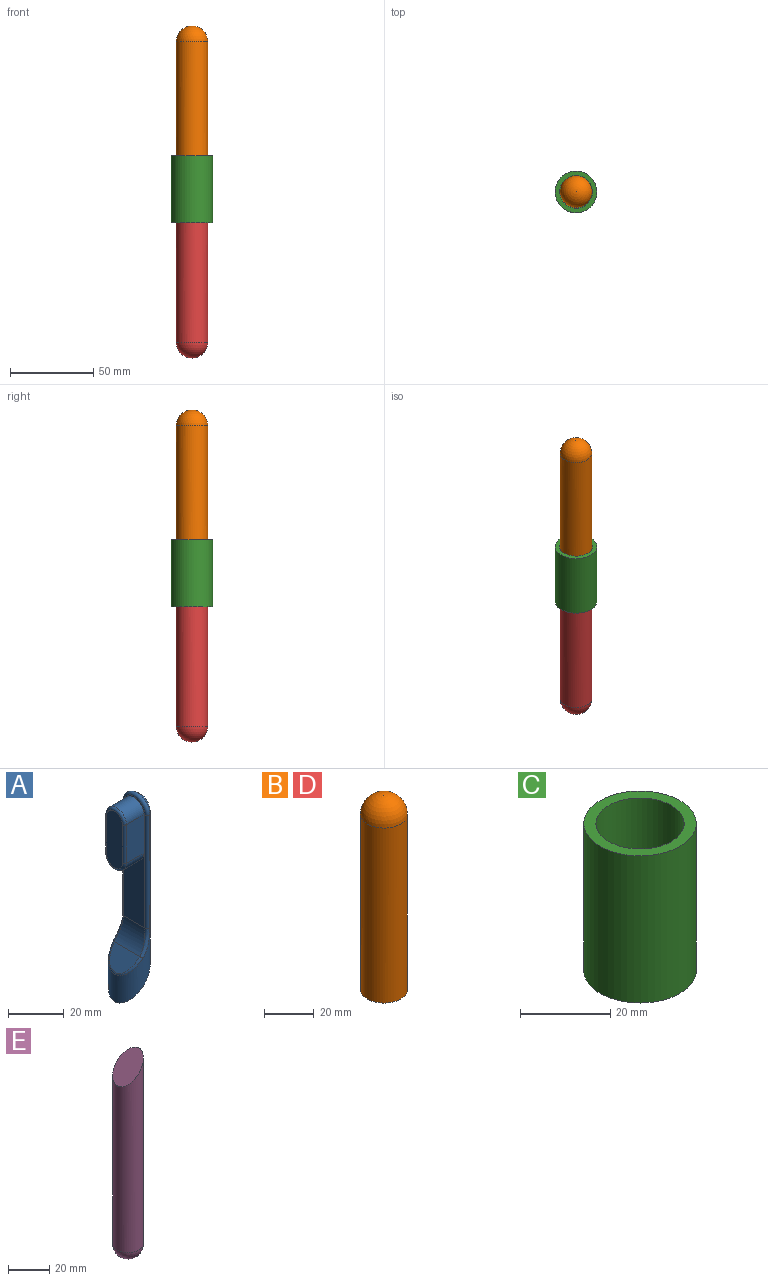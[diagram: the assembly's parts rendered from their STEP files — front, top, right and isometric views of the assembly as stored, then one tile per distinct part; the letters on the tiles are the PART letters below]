
ASSEMBLY  parts=5 mates=4
PART A: 21 faces, bbox 15x15.1x87 mm
  f0: plane 55.28x10.95mm, normal (-1,0,0), area 344.1mm2, adj f4,f5,f7,f9,f12,f13,f14,f15
  f1: cylinder r=7.5mm len=80mm, axis (0,0,-1), area 1400.2mm2, adj f2,f5,f6,f8,f9,f10,f11
  f2: sphere r=7.5mm, area 81.6mm2, adj f1,f7
  f3: plane 12.97x7.21mm, normal (-0.77,0,0.64), area 94.1mm2, adj f4,f8
  f4: cylinder r=15.89mm len=13mm, axis (0,1,0), area 133.2mm2, adj f0,f3,f6,f10
  f5: cylinder r=1mm len=49.8mm, axis (0,0,-1), area 106.5mm2, adj f0,f1,f6,f7
  f6: bspline ~13.34x6.03mm, area 21.9mm2, adj f1,f4,f5,f8
  f7: torus R=5.48mm, axis (1,0,0), area 41.6mm2, adj f0,f2,f5,f9
  f8: bspline ~14.96x7.85mm, area 27.7mm2, adj f1,f3,f6,f10
  f9: cylinder r=1mm len=49.8mm, axis (0,0,-1), area 106.5mm2, adj f0,f1,f7,f10
  f10: bspline ~13.34x6.03mm, area 21.9mm2, adj f1,f4,f8,f9
  f11: plane 15x15mm, normal (0.71,0,-0.71), area 249.9mm2, adj f1
  f12: plane 17x9mm, normal (0,-1,0), area 153mm2, adj f0,f13,f15,f17
  f13: cylinder r=5mm len=10mm, axis (1,0,0), area 141.4mm2, adj f0,f12,f14,f18
  f14: plane 17x9mm, normal (0,1,0), area 153mm2, adj f0,f13,f15,f20
  f15: cylinder r=5mm len=10mm, axis (1,0,0), area 141.4mm2, adj f0,f12,f14,f19
  f16: plane 25x8mm, normal (-1,0,0), area 186.3mm2, adj f17,f18,f19,f20
  f17: cylinder r=1mm len=17mm, axis (0,0,-1), area 26.7mm2, adj f12,f16,f18,f19
  f18: torus R=4mm, axis (-1,0,0), area 22.9mm2, adj f13,f16,f17,f20
  f19: torus R=4mm, axis (-1,0,0), area 22.9mm2, adj f15,f16,f17,f20
  f20: cylinder r=1mm len=17mm, axis (0,0,1), area 26.7mm2, adj f14,f16,f18,f19
PART B: 5 faces, bbox 19x19x96 mm
  f0: cylinder r=9.5mm len=86.5mm, axis (0,0,-1), area 5163.2mm2, adj f1,f2
  f1: plane 19x19mm, normal (0,0,-1), area 56.5mm2, adj f0,f3
  f2: sphere r=9.5mm, area 567.1mm2, adj f0
  f3: cylinder r=8.5mm len=86.5mm, axis (0,0,-1), area 4619.7mm2, adj f1,f4
  f4: sphere r=8.5mm, area 454mm2, adj f3
PART C: 8 faces, bbox 25x25x40 mm
  f0: cylinder r=9.8mm len=19.6mm, axis (0,0,-1), area 923.6mm2, adj f4,f7
  f1: cylinder r=9.8mm len=19.6mm, axis (0,0,-1), area 923.6mm2, adj f3,f6
  f2: cylinder r=12.5mm len=40mm, axis (0,0,-1), area 3141.6mm2, adj f3,f4
  f3: plane 25x25mm, normal (0,0,1), area 189.2mm2, adj f1,f2
  f4: plane 25x25mm, normal (0,0,-1), area 189.2mm2, adj f0,f2
  f5: cylinder r=8.5mm len=17mm, axis (0,0,-1), area 395.2mm2, adj f6,f7
  f6: cone r=8.3mm half-angle=45deg, axis (0,0,1), area 105.7mm2, adj f1,f5
  f7: cone r=9.8mm half-angle=45deg, axis (0,0,-1), area 105.7mm2, adj f0,f5
PART D: same geometry as B
PART E: 3 faces, bbox 15x15x120.6 mm
  f0: sphere r=7.5mm, area 353.4mm2, adj f1
  f1: cylinder r=7.5mm len=113.1mm, axis (0,0,-1), area 4971.6mm2, adj f0,f2
  f2: plane 15x15mm, normal (-0.71,0,0.71), area 249.9mm2, adj f1
PLACE A t=(-10.7,12.64,18.38)mm
PLACE B rot(axis=(0,0,-1),176.2deg) t=(44.09,-22.64,23.05)mm
PLACE C rot(axis=(0,0,1),87.5deg) t=(-80.5,41,21.22)mm
PLACE D rot(axis=(0.69,-0.72,0),180deg) t=(-47.18,66.64,16.22)mm
PLACE E t=(-10.7,12.64,18.38)mm fixed
MATE fastened E.f2 <-> A.f11  axis (-0.71,0,0.71) through (-10.7,12.64,34.88)mm
MATE cylindrical B.f0 <-> E.f1  axis (0,0,-1) through (-10.7,12.64,23.05)mm
MATE cylindrical D.f0 <-> E.f1  axis (0,0,1) through (-10.7,12.64,16.22)mm
MATE fastened C.f0 <-> D.f0  axis (0,0,1) through (-10.7,12.64,16.22)mm
